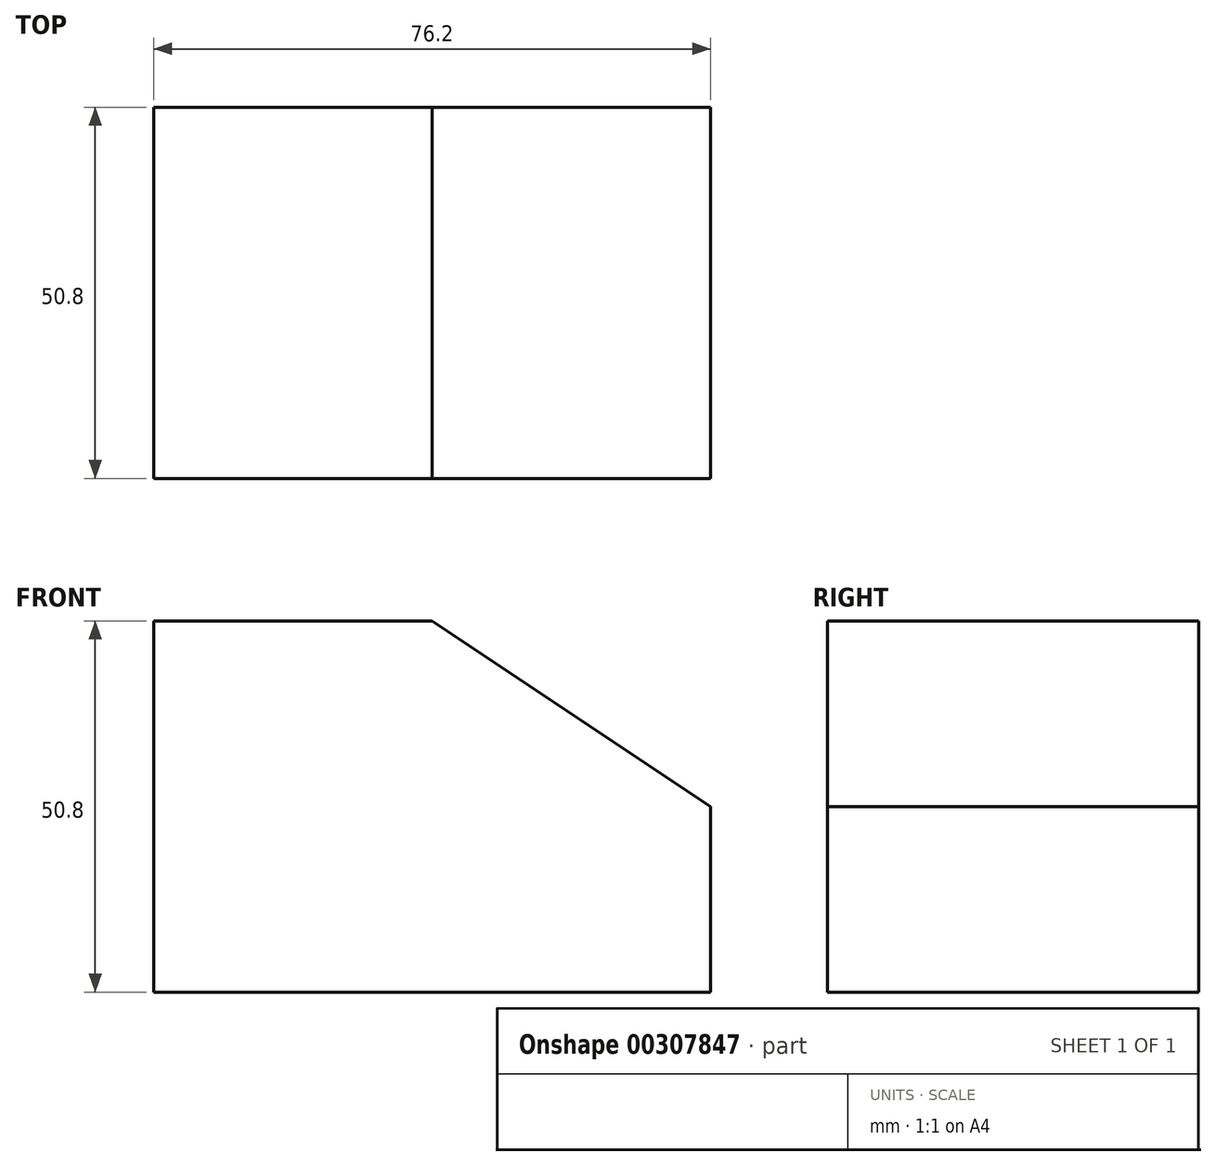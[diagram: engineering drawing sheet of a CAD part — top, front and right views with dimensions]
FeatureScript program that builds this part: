
annotation { "Feature Type Name" : "Feature", "Feature Type Description" : "" }
export const myFeature = defineFeature(function(context is Context, id is Id, definition is map)
    precondition{}
    {
        {
            var Q0;
            Q0=qCreatedBy(makeId("Front.planeOp"),FACE);
            var sketch = newSketch(context, id + "F0", { "sketchPlane" : qUnion([Q0])});
            skLineSegment(sketch, "E0", {"start": v(-17.83, -40.74) * mm, "end": v(58.37, -40.74) * mm});
            skLineSegment(sketch, "E1", {"start": v(58.37, -40.74) * mm, "end": v(58.37, -15.34) * mm});
            skLineSegment(sketch, "E2", {"start": v(58.37, -15.34) * mm, "end": v(20.27, 10.06) * mm});
            skLineSegment(sketch, "E3", {"start": v(20.27, 10.06) * mm, "end": v(-17.83, 10.06) * mm});
            skLineSegment(sketch, "E4", {"start": v(-17.83, 10.06) * mm, "end": v(-17.83, -40.74) * mm});
            skSolve(sketch);
        }
        {
            var Q0;
            Q0=makeQuery(id+"F0.imprint","IMPRINT",FACE,{"disambiguationData":[TD([[makeQuery(id+"F0.imprint","IMPRINT",EDGE,{"derivedFrom":sQuery(id+"F0.wireOp",EDGE,"E0")}),1.0]])]});
            extrude(context, id + "F1", {"entities" : qUnion([Q0]), "depth" : 50.8 * mm});
        }
    });
